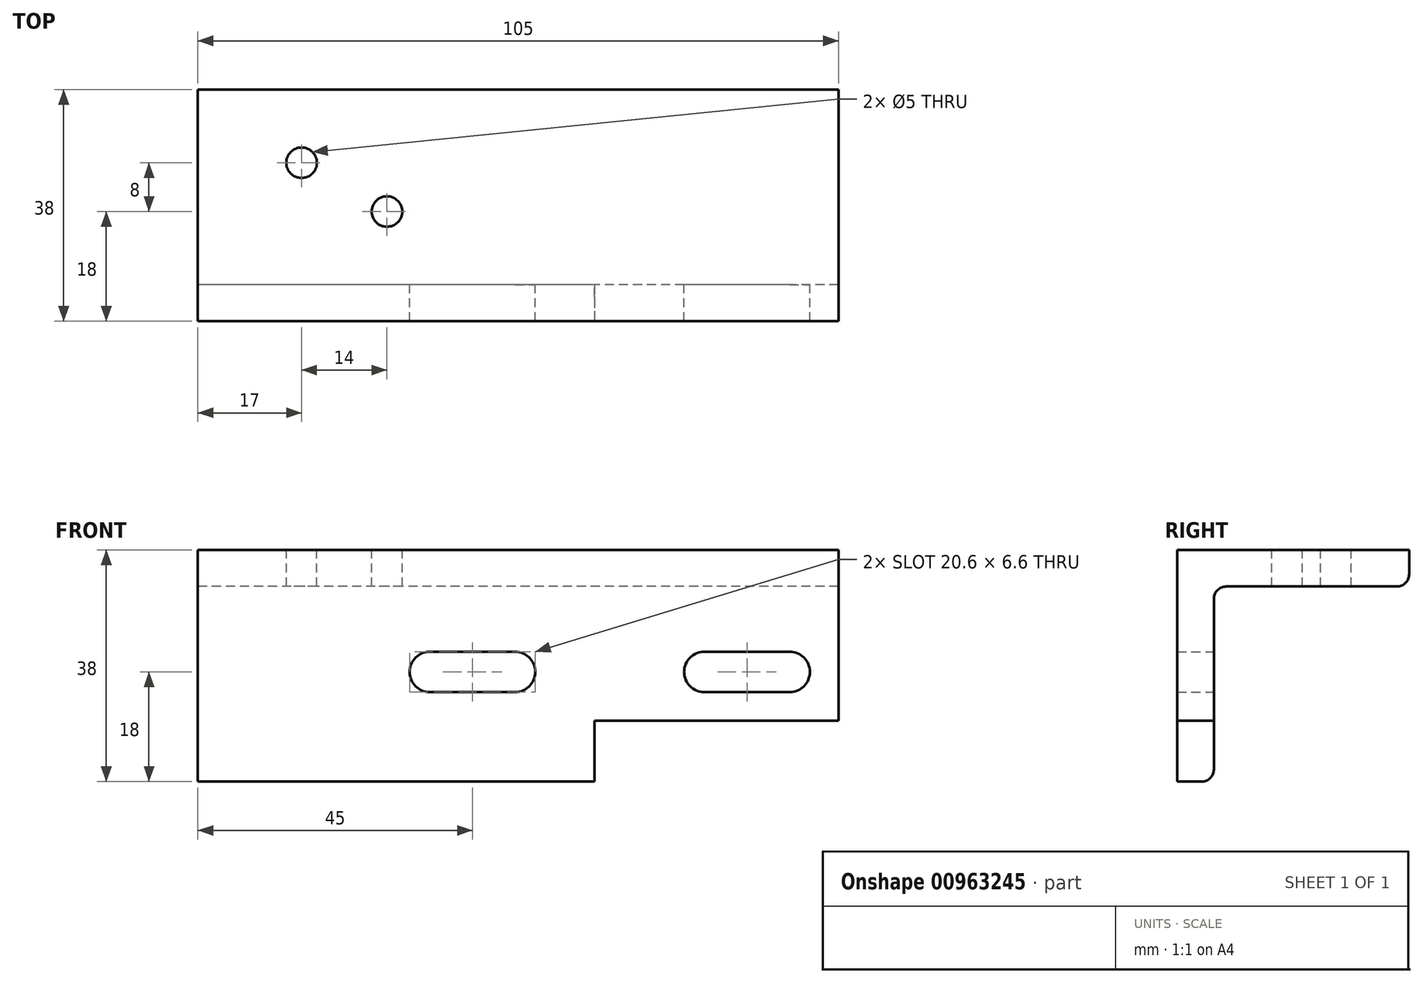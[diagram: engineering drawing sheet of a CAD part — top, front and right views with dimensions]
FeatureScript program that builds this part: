
annotation { "Feature Type Name" : "Feature", "Feature Type Description" : "" }
export const myFeature = defineFeature(function(context is Context, id is Id, definition is map)
    precondition{}
    {
        {
            var Q0;
            Q0=qCreatedBy(makeId("Right.planeOp"),FACE);
            var sketch = newSketch(context, id + "F0", { "sketchPlane" : qUnion([Q0])});
            skLineSegment(sketch, "E0", {"start": v(0, 0) * mm, "end": v(0, 38) * mm});
            skLineSegment(sketch, "E1", {"start": v(0, 38) * mm, "end": v(38, 38) * mm});
            skLineSegment(sketch, "E2", {"start": v(38, 38) * mm, "end": v(38, 32) * mm});
            skLineSegment(sketch, "E3", {"start": v(6, 32) * mm, "end": v(38, 32) * mm});
            skLineSegment(sketch, "E4", {"start": v(6, 32) * mm, "end": v(6, 0) * mm});
            skLineSegment(sketch, "E5", {"start": v(6, 0) * mm, "end": v(0, 0) * mm});
            skSolve(sketch);
        }
        {
            var Q0;
            Q0 = qSketchRegion(id + "F0", true);
            extrude(context, id + "F1", {"entities" : qUnion([Q0]), "depth" : 105 * mm, "offsetDistance" : 25 * mm});
        }
        {
            var Q0;
            Q0=makeQuery(id+"F1.opExtrude","SWEPT_FACE",FACE,{"disambiguationData":[OSD([sQuery(id+"F0.wireOp",EDGE,"E0")])]});
            var sketch = newSketch(context, id + "F2", { "sketchPlane" : qUnion([Q0])});
            skPoint(sketch, "E6", {"position": v(105, 0) * mm});
            skPoint(sketch, "E7", {"position": v(65, 0) * mm});
            skLineSegment(sketch, "E8", {"start": v(65, 0) * mm, "end": v(65, 10) * mm});
            skLineSegment(sketch, "E9", {"start": v(65, 10) * mm, "end": v(105, 10) * mm});
            skPoint(sketch, "E9.endSnap0", {"position": v(105, 19) * mm});
            skLineSegment(sketch, "E10", {"start": v(105, 0) * mm, "end": v(105, 10) * mm});
            skLineSegment(sketch, "E11", {"start": v(105, 0) * mm, "end": v(65, 0) * mm});
            skSolve(sketch);
        }
        {
            var Q0;
            Q0=makeQuery(id+"F2.imprint","IMPRINT",FACE,{"disambiguationData":[TD([[makeQuery(id+"F2.imprint","IMPRINT",EDGE,{"derivedFrom":sQuery(id+"F2.wireOp",EDGE,"E8")}),-1.0]])]});
            extrude(context, id + "F3", {"entities" : qUnion([Q0]), "operationType" : NewBodyOperationType.REMOVE, "oppositeDirection" : true, "depth" : 25 * mm, "offsetDistance" : 25 * mm});
        }
        {
            var Q0;
            Q0=makeQuery(id+"F1.opExtrude","SWEPT_FACE",FACE,{"disambiguationData":[OSD([sQuery(id+"F0.wireOp",EDGE,"E4")])]});
            var sketch = newSketch(context, id + "F4", { "sketchPlane" : qUnion([Q0])});
            skPoint(sketch, "E12", {"position": v(-90, 18) * mm});
            skPoint(sketch, "E12.positionSnap0", {"position": v(-105, 18) * mm});
            skPoint(sketch, "E13", {"position": v(-45, 18) * mm});
            skPoint(sketch, "E14", {"position": v(-97, 18) * mm});
            skPoint(sketch, "E15", {"position": v(-83, 18) * mm});
            skPoint(sketch, "E16", {"position": v(-52, 18) * mm});
            skPoint(sketch, "E17", {"position": v(-38, 18) * mm});
            skCircle(sketch, "E18", {"center": v(-97, 18) * mm, "radius": 3.3 * mm});
            skCircle(sketch, "E19", {"center": v(-83, 18) * mm, "radius": 3.3 * mm});
            skCircle(sketch, "E20", {"center": v(-52, 18) * mm, "radius": 3.3 * mm});
            skCircle(sketch, "E21", {"center": v(-38, 18) * mm, "radius": 3.3 * mm});
            skLineSegment(sketch, "E22", {"start": v(-97, 21.3) * mm, "end": v(-83, 21.3) * mm});
            skLineSegment(sketch, "E23", {"start": v(-83, 21.3) * mm, "end": v(-83, 14.7) * mm});
            skLineSegment(sketch, "E24", {"start": v(-83, 14.7) * mm, "end": v(-97, 14.7) * mm});
            skLineSegment(sketch, "E25", {"start": v(-52, 21.3) * mm, "end": v(-38, 21.3) * mm});
            skLineSegment(sketch, "E26", {"start": v(-38, 21.3) * mm, "end": v(-38, 14.7) * mm});
            skLineSegment(sketch, "E27", {"start": v(-38, 14.7) * mm, "end": v(-52, 14.7) * mm});
            skSolve(sketch);
        }
        {
            var Q0;
            Q0 = qSketchRegion(id + "F4", true);
            extrude(context, id + "F5", {"entities" : qUnion([Q0]), "operationType" : NewBodyOperationType.REMOVE, "oppositeDirection" : true, "depth" : 25 * mm, "offsetDistance" : 25 * mm});
        }
        {
            var Q0;
            Q0=makeQuery(id+"F1.opExtrude","SWEPT_FACE",FACE,{"disambiguationData":[OSD([sQuery(id+"F0.wireOp",EDGE,"E1")])]});
            var sketch = newSketch(context, id + "F6", { "sketchPlane" : qUnion([Q0])});
            skPoint(sketch, "E28", {"position": v(17, 26) * mm});
            skPoint(sketch, "E29", {"position": v(31, 18) * mm});
            skSolve(sketch);
        }
        {
            var Q0;
            Q0=sQuery(id+"F6.wireOp",VERTEX,"E29");
            var Q1;
            Q1=sQuery(id+"F6.wireOp",VERTEX,"E28");
            var Q2;
            Q2=makeQuery(id+"F1.opExtrude","SWEPT_BODY",BODY,{"disambiguationData":[OSD([sQuery(id+"F0.wireOp",EDGE,"E0"),sQuery(id+"F0.wireOp",EDGE,"E1"),sQuery(id+"F0.wireOp",EDGE,"E2"),sQuery(id+"F0.wireOp",EDGE,"E3"),sQuery(id+"F0.wireOp",EDGE,"E4"),sQuery(id+"F0.wireOp",EDGE,"E5")])]});
            hole(context, id + "F7", {"style" : HoleStyle.SIMPLE, "endStyle" : HoleEndStyle.THROUGH, "standardTappedOrClearance" : lookupTablePath({ "standard" : "ISO", "engagement" : "75%", "pitch" : "1 mm", "size" : "M6", "type" : "Tapped" }), "standardBlindInLast" : lookupTablePath({ "standard" : "ISO", "fit" : "Normal", "engagement" : "75%", "pitch" : "1 mm", "size" : "M6", "type" : "Clearance & tapped" }), "holeDiameter" : 5 * mm, "majorDiameter" : 6 * mm, "showTappedDepth" : true, "isTappedThrough" : true, "tappedDepth" : 12.6 * mm, "tapClearance" : 3, "startFromSketch" : true, "locations" : qUnion([Q0, Q1]), "scope" : qUnion([Q2])});
        }
        {
            var Q0;
            Q0=makeQuery(id+"F1.opExtrude","SWEPT_EDGE",EDGE,{"disambiguationData":[OSD([sQuery(id+"F0.wireOp",EDGE,"E2"),sQuery(id+"F0.wireOp",EDGE,"E3")])]});
            var Q1;
            Q1=makeQuery(id+"F1.opExtrude","SWEPT_EDGE",EDGE,{"disambiguationData":[OSD([sQuery(id+"F0.wireOp",EDGE,"E4"),sQuery(id+"F0.wireOp",EDGE,"E5")])]});
            fillet(context, id + "F8", {"entities" : qUnion([Q0, Q1]), "radius" : 2 * mm, "tangentPropagation" : true, "allowEdgeOverflow" : false});
        }
        {
            var Q0;
            Q0=makeQuery(id+"F1.opExtrude","SWEPT_EDGE",EDGE,{"disambiguationData":[OSD([sQuery(id+"F0.wireOp",EDGE,"E3"),sQuery(id+"F0.wireOp",EDGE,"E4")])]});
            fillet(context, id + "F9", {"entities" : qUnion([Q0]), "radius" : 2 * mm, "tangentPropagation" : true, "allowEdgeOverflow" : false});
        }
    });
